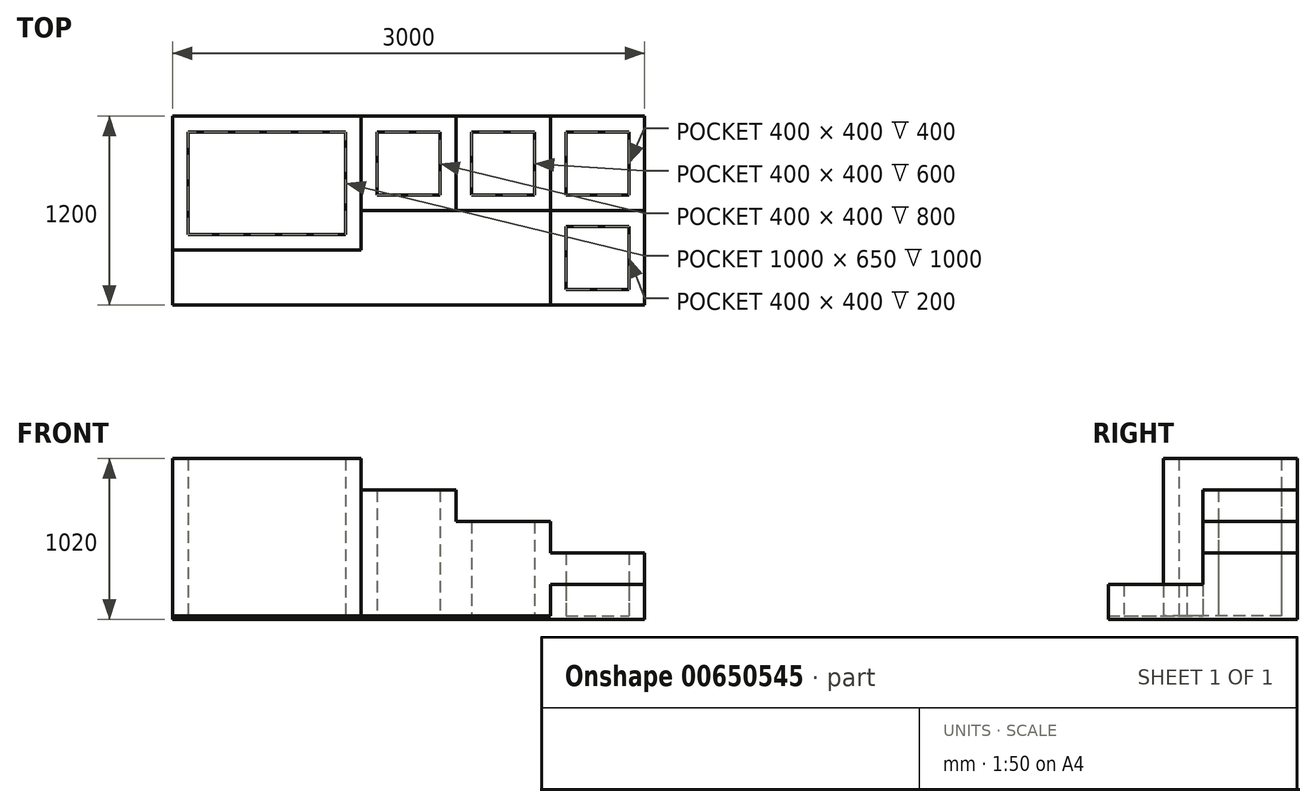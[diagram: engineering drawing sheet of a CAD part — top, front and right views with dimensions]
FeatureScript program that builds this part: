
annotation { "Feature Type Name" : "Feature", "Feature Type Description" : "" }
export const myFeature = defineFeature(function(context is Context, id is Id, definition is map)
    precondition{}
    {
        {
            var Q0;
            Q0=qCreatedBy(makeId("Top.planeOp"),FACE);
            var sketch = newSketch(context, id + "F0", { "sketchPlane" : qUnion([Q0])});
            skLineSegment(sketch, "E0.bottom", {"start": v(0, 0) * mm, "end": v(-2563.64, 0) * mm});
            skLineSegment(sketch, "E0.top", {"start": v(0, 1200) * mm, "end": v(-3000, 1200) * mm});
            skLineSegment(sketch, "E0.left", {"start": v(0, 0) * mm, "end": v(0, 1200) * mm});
            skLineSegment(sketch, "E0.right", {"start": v(-3000, 0) * mm, "end": v(-3000, 1200) * mm});
            skLineSegment(sketch, "E1", {"start": v(-2563.64, 0) * mm, "end": v(-3000, 0) * mm});
            skSolve(sketch);
        }
        {
            var Q0;
            Q0=makeQuery(id+"F0.imprint","IMPRINT",FACE,{"disambiguationData":[TD([[makeQuery(id+"F0.imprint","IMPRINT",EDGE,{"derivedFrom":sQuery(id+"F0.wireOp",EDGE,"E0.bottom")}),-1.0]])]});
            extrude(context, id + "F1", {"entities" : qUnion([Q0]), "depth" : 20 * mm, "offsetDistance" : 25 * mm});
        }
        {
            var Q0;
            Q0=makeQuery(id+"F1.opExtrude","CAP_FACE",FACE,{"disambiguationData":[OSD([sQuery(id+"F0.wireOp",EDGE,"E0.bottom"),sQuery(id+"F0.wireOp",EDGE,"E0.top"),sQuery(id+"F0.wireOp",EDGE,"E0.left"),sQuery(id+"F0.wireOp",EDGE,"E0.right"),sQuery(id+"F0.wireOp",EDGE,"EcOLhzoJ-yrHA-FEvU-6dDI-CAjuHtf4V0fh.bottom"),sQuery(id+"F0.wireOp",EDGE,"EcOLhzoJ-yrHA-FEvU-6dDI-CAjuHtf4V0fh.top"),sQuery(id+"F0.wireOp",EDGE,"EcOLhzoJ-yrHA-FEvU-6dDI-CAjuHtf4V0fh.left"),sQuery(id+"F0.wireOp",EDGE,"EcOLhzoJ-yrHA-FEvU-6dDI-CAjuHtf4V0fh.right")])],"isStart":false});
            var sketch = newSketch(context, id + "F2", { "sketchPlane" : qUnion([Q0])});
            skLineSegment(sketch, "E2.bottom", {"start": v(0, 1200) * mm, "end": v(-600, 1200) * mm});
            skLineSegment(sketch, "E2.top", {"start": v(0, 600) * mm, "end": v(-600, 600) * mm});
            skLineSegment(sketch, "E2.left", {"start": v(0, 1200) * mm, "end": v(0, 600) * mm});
            skLineSegment(sketch, "E2.right", {"start": v(-600, 1200) * mm, "end": v(-600, 600) * mm});
            skLineSegment(sketch, "E3.bottom", {"start": v(-500, 1100) * mm, "end": v(-100, 1100) * mm});
            skLineSegment(sketch, "E3.top", {"start": v(-500, 700) * mm, "end": v(-100, 700) * mm});
            skLineSegment(sketch, "E3.left", {"start": v(-500, 1100) * mm, "end": v(-500, 700) * mm});
            skLineSegment(sketch, "E3.right", {"start": v(-100, 1100) * mm, "end": v(-100, 700) * mm});
            skSolve(sketch);
        }
        {
            var Q0;
            Q0=qSketchRegion(id+"F2",true);
            extrude(context, id + "F3", {"entities" : qUnion([Q0]), "operationType" : NewBodyOperationType.ADD, "depth" : 400 * mm, "offsetDistance" : 25 * mm});
        }
        {
            var Q0;
            {var subQ0=sQuery(id+"F0.wireOp",EDGE,"E0.left");var subQ1=sQuery(id+"F0.wireOp",EDGE,"EcOLhzoJ-yrHA-FEvU-6dDI-CAjuHtf4V0fh.right");var subQ2=sQuery(id+"F0.wireOp",EDGE,"EcOLhzoJ-yrHA-FEvU-6dDI-CAjuHtf4V0fh.left");var subQ3=sQuery(id+"F0.wireOp",EDGE,"EcOLhzoJ-yrHA-FEvU-6dDI-CAjuHtf4V0fh.top");var subQ4=sQuery(id+"F0.wireOp",EDGE,"EcOLhzoJ-yrHA-FEvU-6dDI-CAjuHtf4V0fh.bottom");var subQ5=sQuery(id+"F0.wireOp",EDGE,"E0.bottom");var subQ6=sQuery(id+"F0.wireOp",EDGE,"E0.right");var subQ7=sQuery(id+"F0.wireOp",EDGE,"E0.top");Q0=makeQuery(id+"F3.boolean.opBoolean","SPLIT",FACE,{"disambiguationData":[TD([makeQuery(id+"F1.opExtrude","SWEPT_FACE",FACE,{"disambiguationData":[OSD([subQ5])]})])],"derivedFrom":makeQuery(id+"F1.opExtrude","CAP_FACE",FACE,{"disambiguationData":[OSD([subQ5,subQ7,subQ0,subQ6,subQ4,subQ3,subQ2,subQ1])],"isStart":false})});}
            var sketch = newSketch(context, id + "F4", { "sketchPlane" : qUnion([Q0])});
            skLineSegment(sketch, "E4.bottom", {"start": v(-600, 600) * mm, "end": v(-1200, 600) * mm});
            skLineSegment(sketch, "E4.top", {"start": v(-600, 1200) * mm, "end": v(-1200, 1200) * mm});
            skLineSegment(sketch, "E4.left", {"start": v(-600, 600) * mm, "end": v(-600, 1200) * mm});
            skLineSegment(sketch, "E4.right", {"start": v(-1200, 600) * mm, "end": v(-1200, 1200) * mm});
            skLineSegment(sketch, "E5.bottom", {"start": v(-700, 700) * mm, "end": v(-1100, 700) * mm});
            skLineSegment(sketch, "E5.top", {"start": v(-700, 1100) * mm, "end": v(-1100, 1100) * mm});
            skLineSegment(sketch, "E5.left", {"start": v(-700, 700) * mm, "end": v(-700, 1100) * mm});
            skLineSegment(sketch, "E5.right", {"start": v(-1100, 700) * mm, "end": v(-1100, 1100) * mm});
            skSolve(sketch);
        }
        {
            var Q0;
            Q0=qSketchRegion(id+"F4",true);
            extrude(context, id + "F5", {"entities" : qUnion([Q0]), "operationType" : NewBodyOperationType.ADD, "depth" : 600 * mm, "offsetDistance" : 25 * mm});
        }
        {
            var Q0;
            {var subQ1=sQuery(id+"F0.wireOp",EDGE,"E0.left");var subQ3=sQuery(id+"F0.wireOp",EDGE,"EcOLhzoJ-yrHA-FEvU-6dDI-CAjuHtf4V0fh.right");var subQ5=sQuery(id+"F0.wireOp",EDGE,"EcOLhzoJ-yrHA-FEvU-6dDI-CAjuHtf4V0fh.left");var subQ8=sQuery(id+"F0.wireOp",EDGE,"EcOLhzoJ-yrHA-FEvU-6dDI-CAjuHtf4V0fh.top");var subQ11=sQuery(id+"F0.wireOp",EDGE,"EcOLhzoJ-yrHA-FEvU-6dDI-CAjuHtf4V0fh.bottom");var subQ13=sQuery(id+"F0.wireOp",EDGE,"E0.bottom");var subQ14=makeQuery(id+"F1.opExtrude","SWEPT_FACE",FACE,{"disambiguationData":[OSD([subQ13])]});var subQ15=sQuery(id+"F0.wireOp",EDGE,"E0.right");var subQ17=sQuery(id+"F0.wireOp",EDGE,"E0.top");Q0=makeQuery(id+"F5.boolean.opBoolean","SPLIT",FACE,{"disambiguationData":[TD([subQ14])],"derivedFrom":makeQuery(id+"F3.boolean.opBoolean","SPLIT",FACE,{"disambiguationData":[TD([subQ14])],"derivedFrom":makeQuery(id+"F1.opExtrude","CAP_FACE",FACE,{"disambiguationData":[OSD([subQ13,subQ17,subQ1,subQ15,subQ11,subQ8,subQ5,subQ3])],"isStart":false})})});}
            var sketch = newSketch(context, id + "F6", { "sketchPlane" : qUnion([Q0])});
            skLineSegment(sketch, "E6.bottom", {"start": v(-1200, 600) * mm, "end": v(-1800, 600) * mm});
            skLineSegment(sketch, "E6.top", {"start": v(-1200, 1200) * mm, "end": v(-1800, 1200) * mm});
            skLineSegment(sketch, "E6.left", {"start": v(-1200, 600) * mm, "end": v(-1200, 1200) * mm});
            skLineSegment(sketch, "E6.right", {"start": v(-1800, 600) * mm, "end": v(-1800, 1200) * mm});
            skLineSegment(sketch, "E7.bottom", {"start": v(-1300, 700) * mm, "end": v(-1700, 700) * mm});
            skLineSegment(sketch, "E7.top", {"start": v(-1300, 1100) * mm, "end": v(-1700, 1100) * mm});
            skLineSegment(sketch, "E7.left", {"start": v(-1300, 700) * mm, "end": v(-1300, 1100) * mm});
            skLineSegment(sketch, "E7.right", {"start": v(-1700, 700) * mm, "end": v(-1700, 1100) * mm});
            skSolve(sketch);
        }
        {
            var Q0;
            Q0=qSketchRegion(id+"F6",true);
            extrude(context, id + "F7", {"entities" : qUnion([Q0]), "operationType" : NewBodyOperationType.ADD, "depth" : 800 * mm, "offsetDistance" : 25 * mm});
        }
        {
            var Q0;
            {var subQ1=sQuery(id+"F0.wireOp",EDGE,"E0.left");var subQ3=sQuery(id+"F0.wireOp",EDGE,"EcOLhzoJ-yrHA-FEvU-6dDI-CAjuHtf4V0fh.right");var subQ5=sQuery(id+"F0.wireOp",EDGE,"EcOLhzoJ-yrHA-FEvU-6dDI-CAjuHtf4V0fh.left");var subQ8=sQuery(id+"F0.wireOp",EDGE,"EcOLhzoJ-yrHA-FEvU-6dDI-CAjuHtf4V0fh.top");var subQ11=sQuery(id+"F0.wireOp",EDGE,"EcOLhzoJ-yrHA-FEvU-6dDI-CAjuHtf4V0fh.bottom");var subQ13=sQuery(id+"F0.wireOp",EDGE,"E0.bottom");var subQ14=makeQuery(id+"F1.opExtrude","SWEPT_FACE",FACE,{"disambiguationData":[OSD([subQ13])]});var subQ15=sQuery(id+"F0.wireOp",EDGE,"E0.right");var subQ17=sQuery(id+"F0.wireOp",EDGE,"E0.top");Q0=makeQuery(id+"F7.boolean.opBoolean","SPLIT",FACE,{"disambiguationData":[TD([subQ14])],"derivedFrom":makeQuery(id+"F5.boolean.opBoolean","SPLIT",FACE,{"disambiguationData":[TD([subQ14])],"derivedFrom":makeQuery(id+"F3.boolean.opBoolean","SPLIT",FACE,{"disambiguationData":[TD([subQ14])],"derivedFrom":makeQuery(id+"F1.opExtrude","CAP_FACE",FACE,{"disambiguationData":[OSD([subQ13,subQ17,subQ1,subQ15,subQ11,subQ8,subQ5,subQ3])],"isStart":false})})})});}
            var sketch = newSketch(context, id + "F8", { "sketchPlane" : qUnion([Q0])});
            skLineSegment(sketch, "E8.bottom", {"start": v(-3000, 1200) * mm, "end": v(-1800, 1200) * mm});
            skLineSegment(sketch, "E8.left", {"start": v(-3000, 1200) * mm, "end": v(-3000, 350) * mm});
            skLineSegment(sketch, "E8.right", {"start": v(-1800, 1200) * mm, "end": v(-1800, 350) * mm});
            skLineSegment(sketch, "E9.bottom", {"start": v(-2900, 1100) * mm, "end": v(-1900, 1100) * mm});
            skLineSegment(sketch, "E9.left", {"start": v(-2900, 1100) * mm, "end": v(-2900, 450) * mm});
            skLineSegment(sketch, "E9.right", {"start": v(-1900, 1100) * mm, "end": v(-1900, 450) * mm});
            skLineSegment(sketch, "E10", {"start": v(-2900, 450) * mm, "end": v(-1900, 450) * mm});
            skLineSegment(sketch, "E11", {"start": v(-3000, 350) * mm, "end": v(-1800, 350) * mm});
            skSolve(sketch);
        }
        {
            var Q0;
            Q0=qSketchRegion(id+"F8",true);
            extrude(context, id + "F9", {"entities" : qUnion([Q0]), "operationType" : NewBodyOperationType.ADD, "depth" : 1000 * mm, "offsetDistance" : 25 * mm});
        }
        {
            var Q0;
            {var subQ1=sQuery(id+"F0.wireOp",EDGE,"EcOLhzoJ-yrHA-FEvU-6dDI-CAjuHtf4V0fh.top");var subQ5=sQuery(id+"F0.wireOp",EDGE,"EcOLhzoJ-yrHA-FEvU-6dDI-CAjuHtf4V0fh.left");var subQ7=sQuery(id+"F0.wireOp",EDGE,"EcOLhzoJ-yrHA-FEvU-6dDI-CAjuHtf4V0fh.right");var subQ9=sQuery(id+"F0.wireOp",EDGE,"E1");var subQ10=sQuery(id+"F0.wireOp",EDGE,"E0.bottom");var subQ12=sQuery(id+"F0.wireOp",EDGE,"E0.left");var subQ13=makeQuery(id+"F1.opExtrude","SWEPT_FACE",FACE,{"disambiguationData":[OSD([subQ12])]});var subQ15=sQuery(id+"F0.wireOp",EDGE,"EcOLhzoJ-yrHA-FEvU-6dDI-CAjuHtf4V0fh.bottom");var subQ18=sQuery(id+"F0.wireOp",EDGE,"E0.top");var subQ19=makeQuery(id+"F1.opExtrude","SWEPT_FACE",FACE,{"disambiguationData":[OSD([subQ18])]});var subQ20=sQuery(id+"F0.wireOp",EDGE,"E0.right");Q0=makeQuery(id+"F9.boolean.opBoolean","SPLIT",FACE,{"disambiguationData":[TD([subQ13])],"derivedFrom":makeQuery(id+"F7.boolean.opBoolean","SPLIT",FACE,{"disambiguationData":[TD([subQ19])],"derivedFrom":makeQuery(id+"F5.boolean.opBoolean","SPLIT",FACE,{"disambiguationData":[TD([subQ19])],"derivedFrom":makeQuery(id+"F3.boolean.opBoolean","SPLIT",FACE,{"disambiguationData":[TD([subQ19])],"derivedFrom":makeQuery(id+"F1.opExtrude","CAP_FACE",FACE,{"disambiguationData":[OSD([subQ10,subQ18,subQ12,subQ20,subQ15,subQ1,subQ5,subQ7,subQ9])],"isStart":false})})})})});}
            var sketch = newSketch(context, id + "F10", { "sketchPlane" : qUnion([Q0])});
            skLineSegment(sketch, "E12.bottom", {"start": v(0, 0) * mm, "end": v(-600, 0) * mm});
            skLineSegment(sketch, "E12.top", {"start": v(0, 600) * mm, "end": v(-600, 600) * mm});
            skLineSegment(sketch, "E12.left", {"start": v(0, 0) * mm, "end": v(0, 600) * mm});
            skLineSegment(sketch, "E12.right", {"start": v(-600, 0) * mm, "end": v(-600, 600) * mm});
            skLineSegment(sketch, "E13.bottom", {"start": v(-100, 100) * mm, "end": v(-500, 100) * mm});
            skLineSegment(sketch, "E13.top", {"start": v(-100, 500) * mm, "end": v(-500, 500) * mm});
            skLineSegment(sketch, "E13.left", {"start": v(-100, 100) * mm, "end": v(-100, 500) * mm});
            skLineSegment(sketch, "E13.right", {"start": v(-500, 100) * mm, "end": v(-500, 500) * mm});
            skSolve(sketch);
        }
        {
            var Q0;
            Q0=qSketchRegion(id+"F10",true);
            extrude(context, id + "F11", {"entities" : qUnion([Q0]), "operationType" : NewBodyOperationType.ADD, "depth" : 200 * mm, "offsetDistance" : 25 * mm});
        }
    });
